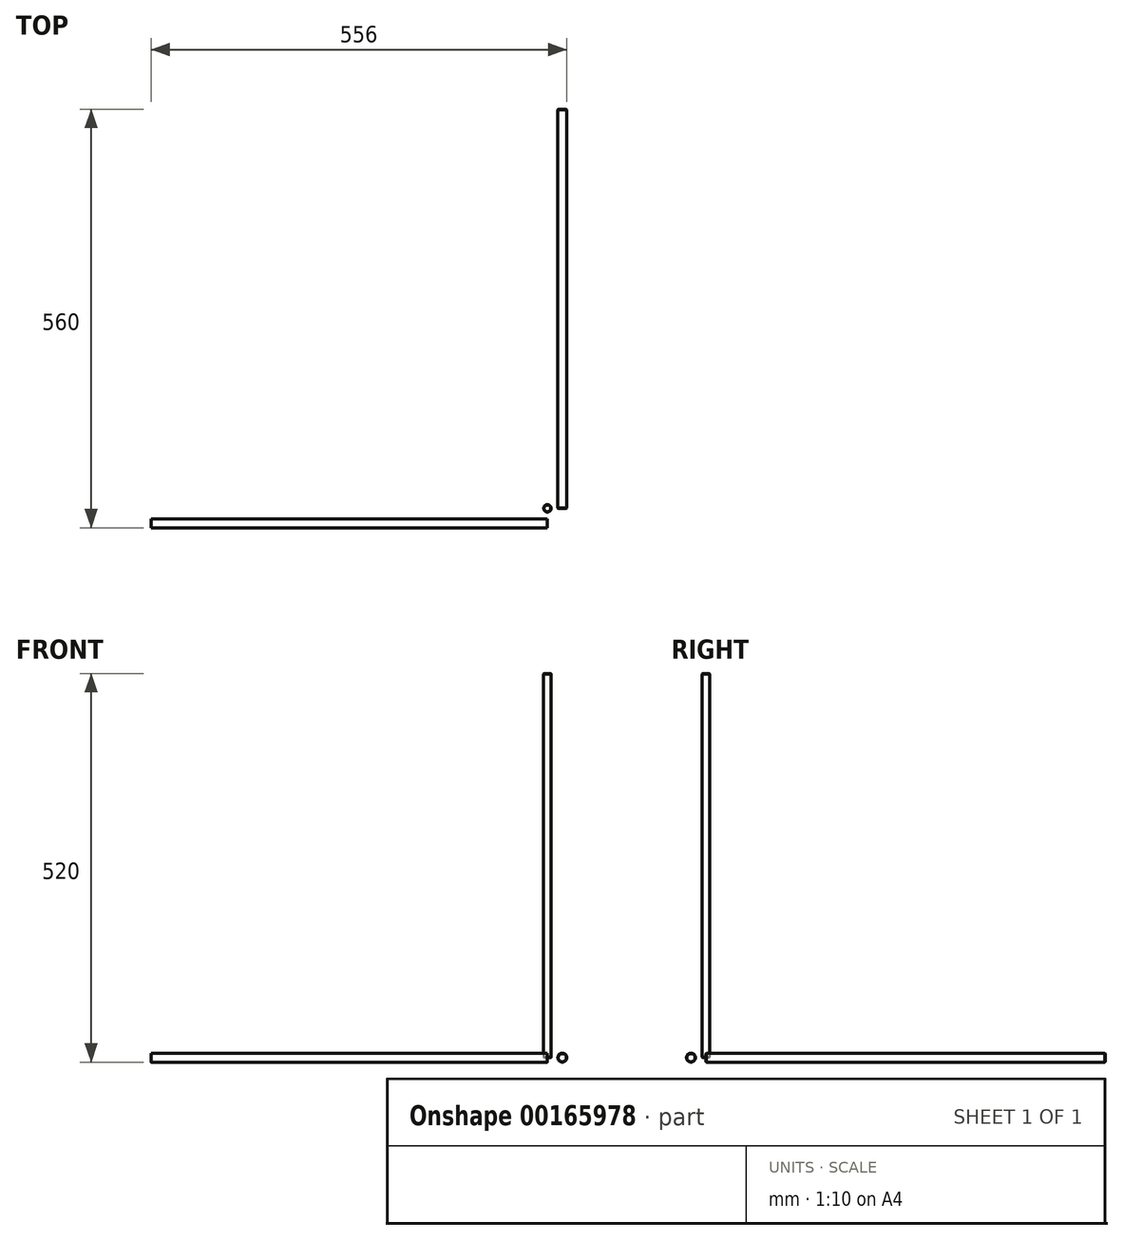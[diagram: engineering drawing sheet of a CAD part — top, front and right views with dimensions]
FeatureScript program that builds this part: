
annotation { "Feature Type Name" : "Feature", "Feature Type Description" : "" }
export const myFeature = defineFeature(function(context is Context, id is Id, definition is map)
    precondition{}
    {
        {
            var Q0;
            Q0=qCreatedBy(makeId("Top.planeOp"),FACE);
            var sketch = newSketch(context, id + "F0", { "sketchPlane" : qUnion([Q0])});
            skCircle(sketch, "E0", {"center": v(0, 0) * mm, "radius": 5 * mm});
            skSolve(sketch);
        }
        {
            var Q0;
            Q0 = qSketchRegion(id + "F0", true);
            extrude(context, id + "F1", {"entities" : qUnion([Q0]), "depth" : 514 * mm});
        }
        {
            var Q0;
            Q0=makeQuery(id+"F1.opExtrude","CAP_EDGE",EDGE,{"disambiguationData":[OSD([sQuery(id+"F0.wireOp",EDGE,"E0")])],"isStart":false});
            var Q1;
            Q1=makeQuery(id+"F1.opExtrude","CAP_EDGE",EDGE,{"disambiguationData":[OSD([sQuery(id+"F0.wireOp",EDGE,"E0")])],"isStart":true});
            chamfer(context, id + "F2", {"entities" : qUnion([Q0, Q1]), "width" : .5 * mm, "tangentPropagation" : true});
        }
        {
            var Q0;
            Q0=qCreatedBy(makeId("Front.planeOp"),FACE);
            var sketch = newSketch(context, id + "F3", { "sketchPlane" : qUnion([Q0])});
            skCircle(sketch, "E1", {"center": v(20, 0) * mm, "radius": 6 * mm});
            skSolve(sketch);
        }
        {
            var Q0;
            Q0 = qSketchRegion(id + "F3", true);
            extrude(context, id + "F4", {"entities" : qUnion([Q0]), "oppositeDirection" : true, "depth" : 534 * mm});
        }
        {
            var Q0;
            Q0=makeQuery(id+"F4.opExtrude","CAP_EDGE",EDGE,{"disambiguationData":[OSD([sQuery(id+"F3.wireOp",EDGE,"E1")])],"isStart":true});
            var Q1;
            Q1=makeQuery(id+"F4.opExtrude","CAP_EDGE",EDGE,{"disambiguationData":[OSD([sQuery(id+"F3.wireOp",EDGE,"E1")])],"isStart":false});
            chamfer(context, id + "F5", {"entities" : qUnion([Q0, Q1]), "width" : .5 * mm, "tangentPropagation" : true});
        }
        {
            var Q0;
            Q0=qCreatedBy(makeId("Right.planeOp"),FACE);
            var sketch = newSketch(context, id + "F6", { "sketchPlane" : qUnion([Q0])});
            skCircle(sketch, "E2", {"center": v(-20, 0) * mm, "radius": 6 * mm});
            skSolve(sketch);
        }
        {
            var Q0;
            Q0 = qSketchRegion(id + "F6", true);
            extrude(context, id + "F7", {"entities" : qUnion([Q0]), "oppositeDirection" : true, "depth" : 530 * mm});
        }
        {
            var Q0;
            Q0=makeQuery(id+"F7.opExtrude","CAP_EDGE",EDGE,{"disambiguationData":[OSD([sQuery(id+"F6.wireOp",EDGE,"E2")])],"isStart":true});
            var Q1;
            Q1=makeQuery(id+"F7.opExtrude","CAP_EDGE",EDGE,{"disambiguationData":[OSD([sQuery(id+"F6.wireOp",EDGE,"E2")])],"isStart":false});
            chamfer(context, id + "F8", {"entities" : qUnion([Q0, Q1]), "width" : .5 * mm, "tangentPropagation" : true});
        }
    });
